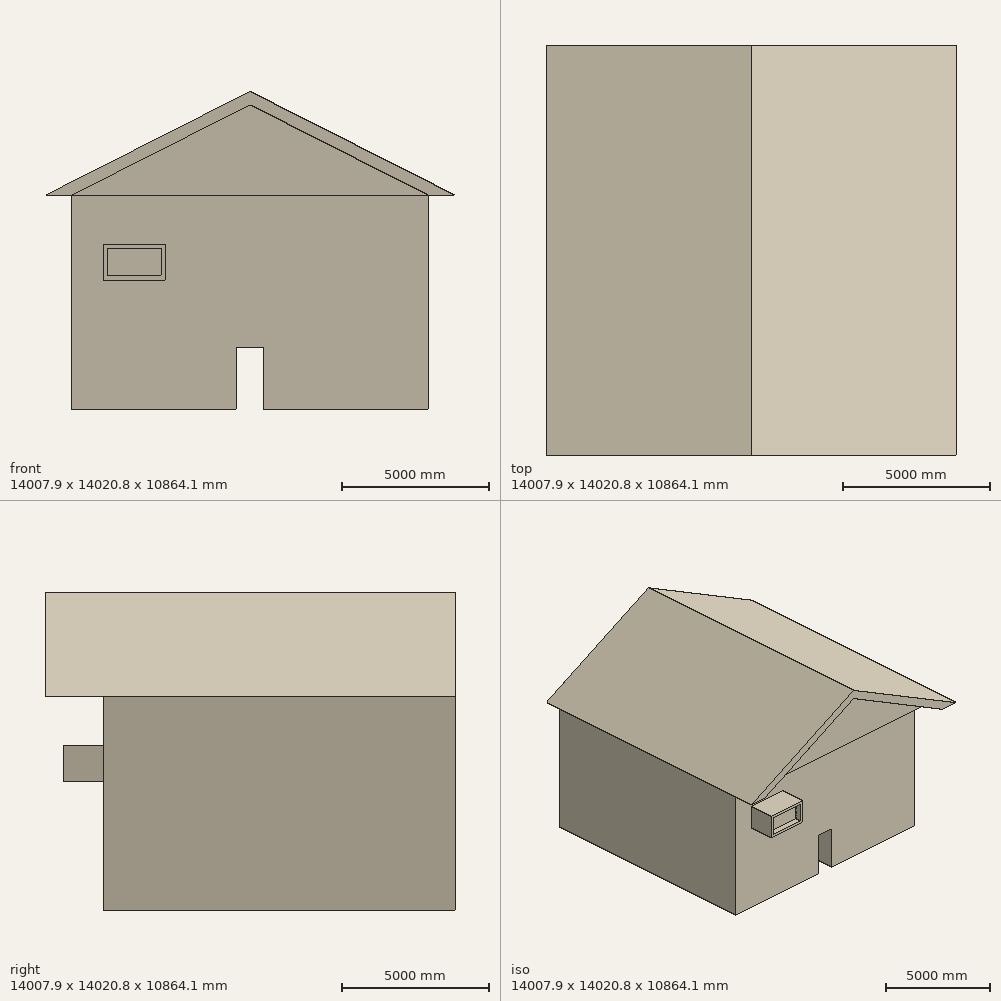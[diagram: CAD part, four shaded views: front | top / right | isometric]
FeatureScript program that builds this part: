
annotation { "Feature Type Name" : "Feature", "Feature Type Description" : "" }
export const myFeature = defineFeature(function(context is Context, id is Id, definition is map)
    precondition{}
    {
        {
            var Q0;
            Q0=qCreatedBy(makeId("Front.planeOp"),FACE);
            var sketch = newSketch(context, id + "F0", { "sketchPlane" : qUnion([Q0])});
            skLineSegment(sketch, "E0", {"start": v(-6096, 0) * mm, "end": v(0, 0) * mm});
            skLineSegment(sketch, "E1", {"start": v(0, 0) * mm, "end": v(6096, 0) * mm});
            skLineSegment(sketch, "E2", {"start": v(6096, 0) * mm, "end": v(0, 0) * mm, "construction": true});
            skLineSegment(sketch, "E3", {"start": v(0, 43.7) * mm, "end": v(0, 0) * mm, "construction": true});
            skLineSegment(sketch, "E4", {"start": v(0, 43.7) * mm, "end": v(0, 3091.7) * mm, "construction": true});
            skLineSegment(sketch, "E5", {"start": v(6096, 0) * mm, "end": v(0, 3091.7) * mm});
            skLineSegment(sketch, "E6", {"start": v(-6096, 0) * mm, "end": v(0, 3091.7) * mm});
            skLineSegment(sketch, "E7", {"start": v(-6096, 0) * mm, "end": v(-7010.4, 0) * mm});
            skLineSegment(sketch, "E8", {"start": v(6096, 0) * mm, "end": v(7010.4, 0) * mm});
            skLineSegment(sketch, "E9", {"start": v(0, 3091.7) * mm, "end": v(0, 3548.9) * mm});
            skLineSegment(sketch, "E10", {"start": v(0, 3548.9) * mm, "end": v(7010.4, 0) * mm});
            skLineSegment(sketch, "E11", {"start": v(0, 3548.9) * mm, "end": v(-7209.06, -107.3) * mm});
            skLineSegment(sketch, "E12", {"start": v(6096, 0) * mm, "end": v(6096, -7315.2) * mm});
            skLineSegment(sketch, "E13", {"start": v(-6096, 0) * mm, "end": v(-6096, -7315.2) * mm});
            skLineSegment(sketch, "E14", {"start": v(-6096, -7315.2) * mm, "end": v(6096, -7315.2) * mm});
            skLineSegment(sketch, "E15", {"start": v(6096, -7315.2) * mm, "end": v(6096, -7620) * mm});
            skLineSegment(sketch, "E16", {"start": v(-6096, -7315.2) * mm, "end": v(-6096, -7620) * mm});
            skLineSegment(sketch, "E17", {"start": v(-6096, -7620) * mm, "end": v(6096, -7620) * mm});
            skLineSegment(sketch, "E18", {"start": v(0, 0) * mm, "end": v(0, -7315.2) * mm, "construction": true});
            skLineSegment(sketch, "E19", {"start": v(0, -7315.2) * mm, "end": v(457.2, -7315.2) * mm});
            skLineSegment(sketch, "E20", {"start": v(457.2, -7315.2) * mm, "end": v(0, -7315.2) * mm});
            skLineSegment(sketch, "E21", {"start": v(0, -7315.2) * mm, "end": v(-457.2, -7315.2) * mm});
            skLineSegment(sketch, "E22.bottom", {"start": v(-4876.8, -1828.8) * mm, "end": v(-3048, -1828.8) * mm});
            skLineSegment(sketch, "E22.top", {"start": v(-4876.8, -2743.2) * mm, "end": v(-3048, -2743.2) * mm});
            skLineSegment(sketch, "E22.left", {"start": v(-4876.8, -1828.8) * mm, "end": v(-4876.8, -2743.2) * mm});
            skLineSegment(sketch, "E22.right", {"start": v(-3048, -1828.8) * mm, "end": v(-3048, -2743.2) * mm});
            skLineSegment(sketch, "E23.0", {"start": v(-5029.2, -1676.4) * mm, "end": v(-2895.6, -1676.4) * mm});
            skLineSegment(sketch, "E23.1", {"start": v(-5029.2, -1676.4) * mm, "end": v(-5029.2, -2895.6) * mm});
            skLineSegment(sketch, "E23.2", {"start": v(-5029.2, -2895.6) * mm, "end": v(-2895.6, -2895.6) * mm});
            skLineSegment(sketch, "E23.3", {"start": v(-2895.6, -1676.4) * mm, "end": v(-2895.6, -2895.6) * mm});
            skLineSegment(sketch, "E24", {"start": v(-457.2, -7315.2) * mm, "end": v(-457.2, -5181.6) * mm});
            skLineSegment(sketch, "E25", {"start": v(-457.2, -5181.6) * mm, "end": v(457.2, -5181.6) * mm});
            skLineSegment(sketch, "E26", {"start": v(457.2, -5181.6) * mm, "end": v(457.2, -7315.2) * mm});
            skSolve(sketch);
        }
        {
            var Q0;
            {var subQ0=sQuery(id+"F0.wireOp",EDGE,"E6");Q0=makeQuery(id+"F0.imprint","IMPRINT",FACE,{"disambiguationData":[TD([[makeQuery(id+"F0.imprint","IMPRINT",EDGE,{"derivedFrom":subQ0}),1.0]])]});}
            var Q1;
            Q1=makeQuery(id+"F0.imprint","IMPRINT",FACE,{"disambiguationData":[TD([[makeQuery(id+"F0.imprint","IMPRINT",EDGE,{"derivedFrom":sQuery(id+"F0.wireOp",EDGE,"E5")}),-1.0]])]});
            extrude(context, id + "F1", {"entities" : qUnion([Q0, Q1]), "depth" : 14020.8 * mm, "offsetDistance" : 30.48 * mm});
        }
        {
            var Q0;
            Q0=makeQuery(id+"F0.imprint","IMPRINT",FACE,{"disambiguationData":[TD([[makeQuery(id+"F0.imprint","IMPRINT",EDGE,{"derivedFrom":sQuery(id+"F0.wireOp",EDGE,"E0")}),1.0]])]});
            extrude(context, id + "F2", {"entities" : qUnion([Q0]), "operationType" : NewBodyOperationType.ADD, "depth" : 13106.4 * mm, "offsetDistance" : 30.48 * mm});
        }
        {
            var Q0;
            Q0=makeQuery(id+"F0.imprint","IMPRINT",FACE,{"disambiguationData":[TD([[makeQuery(id+"F0.imprint","IMPRINT",EDGE,{"derivedFrom":sQuery(id+"F0.wireOp",EDGE,"E0")}),-1.0]])]});
            extrude(context, id + "F3", {"entities" : qUnion([Q0]), "operationType" : NewBodyOperationType.ADD, "depth" : 12039.6 * mm, "offsetDistance" : 30.48 * mm});
        }
        {
            var Q0;
            Q0=sQuery(id+"F0.wireOp",EDGE,"E17");
            extrude(context, id + "F4", {"bodyType" : ToolBodyType.SURFACE, "surfaceEntities" : qUnion([Q0]), "depth" : 13106.4 * mm, "offsetDistance" : 30.48 * mm});
        }
        {
            var Q0;
            Q0=makeQuery(id+"F0.imprint","IMPRINT",FACE,{"disambiguationData":[TD([[makeQuery(id+"F0.imprint","IMPRINT",EDGE,{"derivedFrom":sQuery(id+"F0.wireOp",EDGE,"E22.bottom")}),-1.0]])]});
            extrude(context, id + "F5", {"entities" : qUnion([Q0]), "depth" : 13106.4 * mm, "offsetDistance" : 30.48 * mm});
        }
        {
            var Q0;
            Q0=makeQuery(id+"F0.imprint","IMPRINT",FACE,{"disambiguationData":[TD([[makeQuery(id+"F0.imprint","IMPRINT",EDGE,{"derivedFrom":sQuery(id+"F0.wireOp",EDGE,"E22.bottom")}),1.0]])]});
            extrude(context, id + "F6", {"entities" : qUnion([Q0]), "depth" : 13411.2 * mm, "offsetDistance" : 30.48 * mm});
        }
    });
